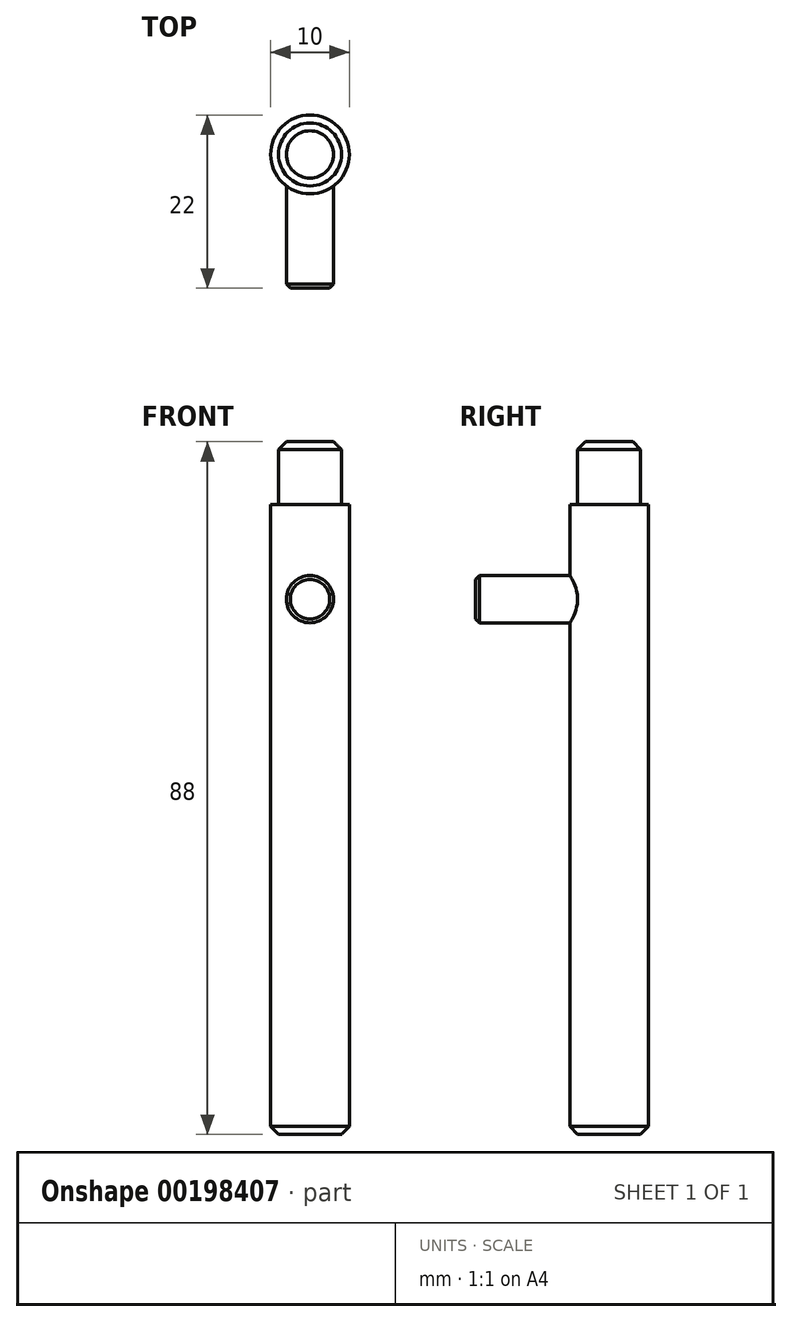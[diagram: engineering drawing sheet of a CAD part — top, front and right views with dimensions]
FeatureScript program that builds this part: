
annotation { "Feature Type Name" : "Feature", "Feature Type Description" : "" }
export const myFeature = defineFeature(function(context is Context, id is Id, definition is map)
    precondition{}
    {
        {
            var Q0;
            Q0=qCreatedBy(makeId("Top.planeOp"),FACE);
            var sketch = newSketch(context, id + "F0", { "sketchPlane" : qUnion([Q0])});
            skCircle(sketch, "E0", {"center": v(0, 0) * mm, "radius": 4 * mm});
            skCircle(sketch, "E1", {"center": v(0, 0) * mm, "radius": 5 * mm});
            skSolve(sketch);
        }
        {
            var Q0;
            Q0=makeQuery(id+"F0.imprint","IMPRINT",FACE,{"disambiguationData":[TD([[makeQuery(id+"F0.imprint","IMPRINT",EDGE,{"derivedFrom":sQuery(id+"F0.wireOp",EDGE,"E0")}),1.0]])]});
            extrude(context, id + "F1", {"entities" : qUnion([Q0]), "depth" : 8 * mm, "hasSecondDirection" : true, "secondDirectionOppositeDirection" : true, "secondDirectionDepth" : 80 * mm});
        }
        {
            var Q0;
            Q0 = qSketchRegion(id + "F0", true);
            extrude(context, id + "F2", {"entities" : qUnion([Q0]), "oppositeDirection" : true, "depth" : 80 * mm});
        }
        {
            var Q0;
            Q0=qCreatedBy(makeId("Front.planeOp"),FACE);
            var sketch = newSketch(context, id + "F3", { "sketchPlane" : qUnion([Q0])});
            skCircle(sketch, "E2", {"center": v(0, -12) * mm, "radius": 3 * mm});
            skSolve(sketch);
        }
        {
            var Q0;
            Q0 = qSketchRegion(id + "F3", true);
            extrude(context, id + "F4", {"entities" : qUnion([Q0]), "operationType" : NewBodyOperationType.ADD, "depth" : 17 * mm});
        }
        {
            var Q0;
            Q0=makeQuery(id+"F2.opExtrude","CAP_EDGE",EDGE,{"disambiguationData":[OSD([sQuery(id+"F0.wireOp",EDGE,"E1")])],"isStart":false});
            var Q1;
            Q1=makeQuery(id+"F1.opExtrude","CAP_EDGE",EDGE,{"disambiguationData":[OSD([sQuery(id+"F0.wireOp",EDGE,"E0")])],"isStart":false});
            chamfer(context, id + "F5", {"entities" : qUnion([Q0, Q1]), "width" : 1 * mm, "tangentPropagation" : true});
        }
        {
            var Q0;
            Q0=makeQuery(id+"F4.opExtrude","CAP_EDGE",EDGE,{"disambiguationData":[OSD([sQuery(id+"F3.wireOp",EDGE,"E2")])],"isStart":false});
            chamfer(context, id + "F6", {"entities" : qUnion([Q0]), "width" : .5 * mm, "tangentPropagation" : true});
        }
    });
